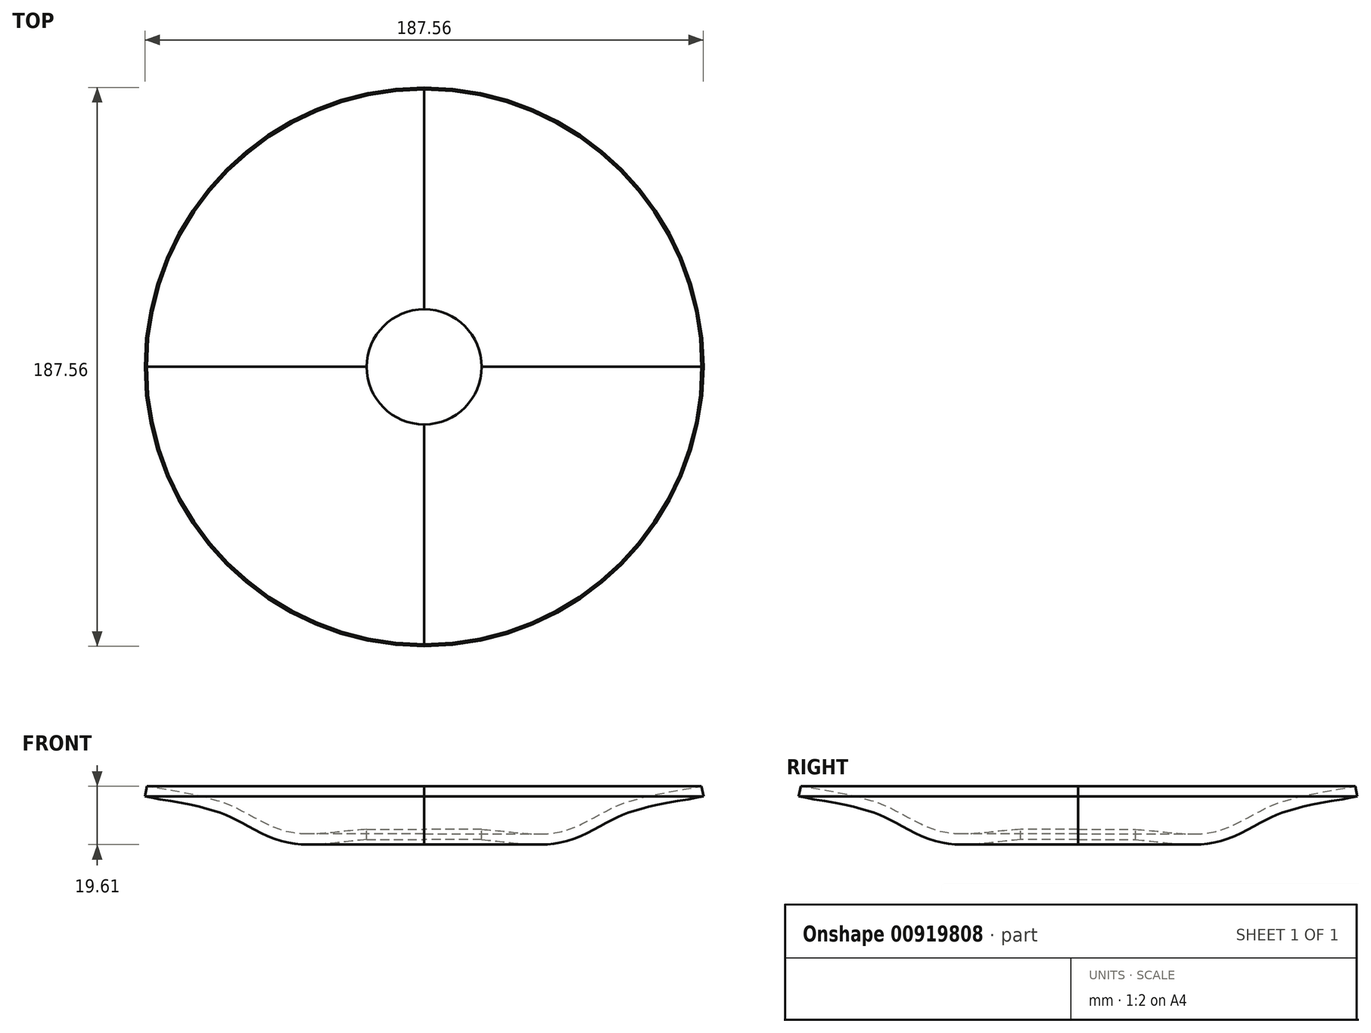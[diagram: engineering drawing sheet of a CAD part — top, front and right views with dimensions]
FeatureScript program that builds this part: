
annotation { "Feature Type Name" : "Feature", "Feature Type Description" : "" }
export const myFeature = defineFeature(function(context is Context, id is Id, definition is map)
    precondition{}
    {
        {
            var Q0;
            Q0=qCreatedBy(makeId("Front.planeOp"),FACE);
            var sketch = newSketch(context, id + "F0", { "sketchPlane" : qUnion([Q0])});
            skFitSpline(sketch, "E0", {"points": [v(0, 0) * mm, v(43.28, 0) * mm, v(64.5, 9.04) * mm, v(93.14, 15.77) * mm], "startDerivative": vector(129.42, 30.3) * mm, "endDerivative": vector(106.08, 19.66) * mm});
            skFitSpline(sketch, "E1.0", {"points": [v(0.8, -3.43) * mm, v(3.31, -2.85) * mm, v(8.27, -2.11) * mm, v(15.53, -1.99) * mm, v(22.58, -2.48) * mm, v(28.25, -3.1) * mm, v(32.65, -3.52) * mm, v(35.88, -3.75) * mm, v(39.05, -3.84) * mm, v(41.64, -3.74) * mm, v(43.68, -3.52) * mm, v(45.7, -3.2) * mm, v(48.08, -2.62) * mm, v(50.77, -1.7) * mm, v(53.3, -0.64) * mm, v(55.7, 0.52) * mm, v(58, 1.73) * mm, v(60.2, 2.94) * mm, v(62.36, 4.1) * mm, v(64.13, 5) * mm, v(65.55, 5.64) * mm, v(66.96, 6.25) * mm, v(68.8, 6.95) * mm, v(71.1, 7.7) * mm, v(73.5, 8.37) * mm, v(76.87, 9.19) * mm, v(81.37, 10.1) * mm, v(87.27, 11.14) * mm, v(91.55, 11.9) * mm, v(93.78, 12.3) * mm]});
            skLineSegment(sketch, "E2", {"start": v(93.14, 15.77) * mm, "end": v(93.78, 12.3) * mm});
            skLineSegment(sketch, "E3", {"start": v(0, 0) * mm, "end": v(0, -3.43) * mm});
            skLineSegment(sketch, "E4", {"start": v(0, -3.43) * mm, "end": v(0.8, -3.43) * mm});
            skLineSegment(sketch, "E5", {"start": v(0.8, 15.77) * mm, "end": v(0, -31.03) * mm});
            skSolve(sketch);
        }
        {
            var Q0;
            {var subQ1=sQuery(id+"F0.wireOp",EDGE,"E1.0");Q0=makeQuery(id+"F0.imprint","IMPRINT",FACE,{"disambiguationData":[TD([[makeQuery(id+"F0.imprint","IMPRINT",EDGE,{"derivedFrom":subQ1}),1.0]])]});}
            var Q1;
            Q1=sQuery(id+"F0.wireOp",EDGE,"E3");
            revolve(context, id + "F1", {"surfaceOperationType" : NewSurfaceOperationType.NEW, "entities" : qUnion([Q0]), "axis" : qUnion([Q1]), "revolveType" : RevolveType.ONE_DIRECTION, "angle" : 90 * degree});
        }
        {
            var Q0;
            Q0=qCreatedBy(makeId("Top.planeOp"),FACE);
            var sketch = newSketch(context, id + "F2", { "sketchPlane" : qUnion([Q0])});
            skCircle(sketch, "E6", {"center": v(0, 0) * mm, "radius": 19.32 * mm});
            skSolve(sketch);
        }
        {
            var Q0;
            Q0 = qSketchRegion(id + "F2", true);
            extrude(context, id + "F3", {"entities" : qUnion([Q0]), "operationType" : NewBodyOperationType.REMOVE, "endBound" : BoundingType.SYMMETRIC, "oppositeDirection" : true, "depth" : 25 * mm, "offsetDistance" : 25 * mm});
        }
        {
            var Q0;
            Q0=makeQuery(id+"F1.opRevolve","SWEPT_BODY",BODY,{"disambiguationData":[OSD([sQuery(id+"F0.wireOp",EDGE,"E0"),sQuery(id+"F0.wireOp",EDGE,"E1.0"),sQuery(id+"F0.wireOp",EDGE,"E2"),sQuery(id+"F0.wireOp",EDGE,"E4"),sQuery(id+"F0.wireOp",EDGE,"E5")])]});
            var Q1;
            Q1=makeQuery(id+"F3.boolean.opBoolean","COPY",FACE,{"derivedFrom":makeQuery(id+"F3.opExtrude","SWEPT_FACE",FACE,{"disambiguationData":[OSD([sQuery(id+"F2.wireOp",EDGE,"E6")])]})});
            circularPattern(context, id + "F4", {"entities" : qUnion([Q0]), "axis" : qUnion([Q1]), "angle" : 360 * degree, "instanceCount" : 4, "equalSpace" : true});
        }
    });
